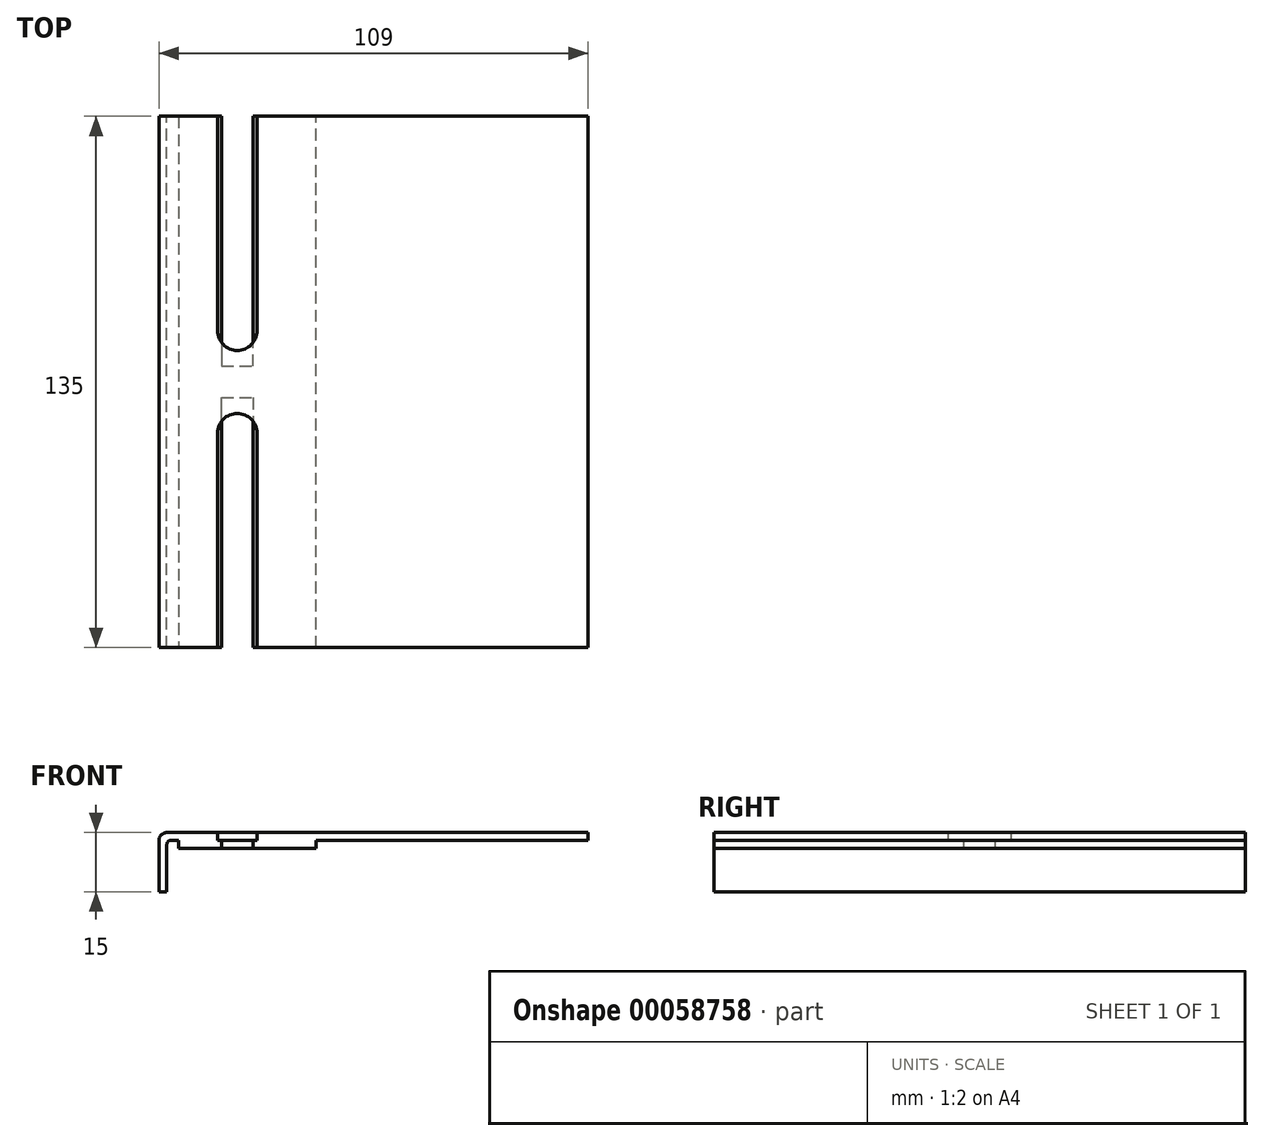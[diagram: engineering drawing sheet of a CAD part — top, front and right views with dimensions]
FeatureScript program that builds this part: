
annotation { "Feature Type Name" : "Feature", "Feature Type Description" : "" }
export const myFeature = defineFeature(function(context is Context, id is Id, definition is map)
    precondition{}
    {
        {
            var Q0;
            Q0=qCreatedBy(makeId("Front.planeOp"),FACE);
            var sketch = newSketch(context, id + "F0", { "sketchPlane" : qUnion([Q0])});
            skLineSegment(sketch, "E0.rect.bottom", {"start": v(54.5, -1) * mm, "end": v(-51.5, -1) * mm});
            skLineSegment(sketch, "E0.rect.top", {"start": v(54.5, 1) * mm, "end": v(-52.5, 1) * mm});
            skLineSegment(sketch, "E0.rect.left", {"start": v(54.5, -1) * mm, "end": v(54.5, 1) * mm});
            skPoint(sketch, "E0.rect.middle", {"position": v(0, 0) * mm});
            skLineSegment(sketch, "E1.top", {"start": v(-54.5, -14) * mm, "end": v(-52.5, -14) * mm});
            skLineSegment(sketch, "E1.right", {"start": v(-52.5, -2) * mm, "end": v(-52.5, -14) * mm});
            skLineSegment(sketch, "E2", {"start": v(-54.5, -1) * mm, "end": v(-54.5, -14) * mm});
            skPoint(sketch, "E3.visualSharp", {"position": v(-54.5, 1) * mm});
            skArc(sketch, "E3.filletArc", {"start": v(-52.5, 1) * mm, "mid": v(-53.91, 0.41) * mm, "end": v(-54.5, -1) * mm});
            skArc(sketch, "E4.filletArc", {"start": v(-51.5, -1) * mm, "mid": v(-52.2, -1.3) * mm, "end": v(-52.5, -2) * mm});
            skSolve(sketch);
        }
        {
            var Q0;
            Q0=makeQuery(id+"F0.imprint","IMPRINT",FACE,{"disambiguationData":[TD([[makeQuery(id+"F0.imprint","IMPRINT",EDGE,{"derivedFrom":sQuery(id+"F0.wireOp",EDGE,"E0.rect.bottom")}),-1.0]])]});
            extrude(context, id + "F1", {"entities" : qUnion([Q0]), "depth" : 67.5 * mm, "hasSecondDirection" : true, "secondDirectionOppositeDirection" : true, "secondDirectionDepth" : 67.5 * mm});
        }
        {
            var Q0;
            Q0=makeQuery(id+"F1.opExtrude","SWEPT_FACE",FACE,{"disambiguationData":[OSD([sQuery(id+"F0.wireOp",EDGE,"E0.rect.top")])]});
            var sketch = newSketch(context, id + "F2", { "sketchPlane" : qUnion([Q0])});
            skLineSegment(sketch, "E5.bottom", {"start": v(-34.6, 8) * mm, "end": v(-34.6, 8) * mm});
            skLineSegment(sketch, "E5.top", {"start": v(-39.6, 67.5) * mm, "end": v(-29.6, 67.5) * mm});
            skLineSegment(sketch, "E5.left", {"start": v(-39.6, 13) * mm, "end": v(-39.6, 67.5) * mm});
            skLineSegment(sketch, "E5.right", {"start": v(-29.6, 13) * mm, "end": v(-29.6, 67.5) * mm});
            skLineSegment(sketch, "E6.bottom", {"start": v(-34.6, -8) * mm, "end": v(-34.6, -8) * mm});
            skLineSegment(sketch, "E6.top", {"start": v(-39.6, -67.5) * mm, "end": v(-29.6, -67.5) * mm});
            skLineSegment(sketch, "E6.left", {"start": v(-39.6, -13) * mm, "end": v(-39.6, -67.5) * mm});
            skLineSegment(sketch, "E6.right", {"start": v(-29.6, -13) * mm, "end": v(-29.6, -67.5) * mm});
            skPoint(sketch, "E7.visualSharp", {"position": v(-39.6, 8) * mm});
            skArc(sketch, "E7.filletArc", {"start": v(-39.6, 13) * mm, "mid": v(-38.14, 9.46) * mm, "end": v(-34.6, 8) * mm});
            skPoint(sketch, "E8.visualSharp", {"position": v(-29.6, 8) * mm});
            skArc(sketch, "E8.filletArc", {"start": v(-34.6, 8) * mm, "mid": v(-31.06, 9.46) * mm, "end": v(-29.6, 13) * mm});
            skPoint(sketch, "E9.visualSharp", {"position": v(-39.6, -8) * mm});
            skArc(sketch, "E9.filletArc", {"start": v(-34.6, -8) * mm, "mid": v(-38.14, -9.46) * mm, "end": v(-39.6, -13) * mm});
            skPoint(sketch, "E10.visualSharp", {"position": v(-29.6, -8) * mm});
            skArc(sketch, "E10.filletArc", {"start": v(-29.6, -13) * mm, "mid": v(-31.06, -9.46) * mm, "end": v(-34.6, -8) * mm});
            skSolve(sketch);
        }
        {
            var Q0;
            Q0=makeQuery(id+"F2.imprint","IMPRINT",FACE,{"disambiguationData":[TD([[makeQuery(id+"F2.imprint","IMPRINT",EDGE,{"derivedFrom":sQuery(id+"F2.wireOp",EDGE,"E6.top")}),-1.0]])]});
            var Q1;
            Q1=makeQuery(id+"F2.imprint","IMPRINT",FACE,{"disambiguationData":[TD([[makeQuery(id+"F2.imprint","IMPRINT",EDGE,{"derivedFrom":sQuery(id+"F2.wireOp",EDGE,"E5.top")}),1.0]])]});
            extrude(context, id + "F3", {"entities" : qUnion([Q0, Q1]), "operationType" : NewBodyOperationType.REMOVE, "endBound" : BoundingType.THROUGH_ALL, "oppositeDirection" : true, "depth" : 25 * mm});
        }
        {
            var Q0;
            Q0=makeQuery(id+"F1.opExtrude","SWEPT_FACE",FACE,{"disambiguationData":[OSD([sQuery(id+"F0.wireOp",EDGE,"E0.rect.bottom")])]});
            var sketch = newSketch(context, id + "F4", { "sketchPlane" : qUnion([Q0])});
            skLineSegment(sketch, "E11", {"start": v(-49.5, 67.5) * mm, "end": v(-38.6, 67.5) * mm});
            skLineSegment(sketch, "E12", {"start": v(-38.6, 67.5) * mm, "end": v(-38.6, 4) * mm});
            skLineSegment(sketch, "E13", {"start": v(-38.6, 4) * mm, "end": v(-30.6, 4) * mm});
            skLineSegment(sketch, "E14", {"start": v(-30.6, 4) * mm, "end": v(-30.6, 67.5) * mm});
            skLineSegment(sketch, "E15", {"start": v(-30.6, 67.5) * mm, "end": v(-14.6, 67.5) * mm});
            skLineSegment(sketch, "E16", {"start": v(-14.6, 67.5) * mm, "end": v(-14.6, 0) * mm});
            skLineSegment(sketch, "E17", {"start": v(-14.6, 0) * mm, "end": v(-49.5, 0) * mm});
            skLineSegment(sketch, "E18", {"start": v(-49.5, 0) * mm, "end": v(-49.5, 67.5) * mm});
            skSolve(sketch);
        }
        {
            var Q0;
            {var subQ16=sQuery(id+"F4.wireOp",EDGE,"E13");Q0=makeQuery(id+"F4.imprint","IMPRINT",FACE,{"disambiguationData":[TD([[makeQuery(id+"F4.imprint","IMPRINT",EDGE,{"derivedFrom":subQ16}),-1.0]])]});}
            var Q1;
            {var subQ1=makeQuery(id+"F1.opExtrude","SWEPT_FACE",FACE,{"disambiguationData":[OSD([sQuery(id+"F0.wireOp",EDGE,"E0.rect.bottom")])]});var subQ2=makeQuery(id+"F3.boolean.opBoolean","INTERSECT",EDGE,{"derivedFrom":[subQ1,makeQuery(id+"F3.opExtrude","SWEPT_FACE",FACE,{"disambiguationData":[OSD([sQuery(id+"F2.wireOp",EDGE,"E6.left")])]})]});Q1=makeQuery(id+"F4.imprint","IMPRINT",FACE,{"disambiguationData":[TD([[makeQuery(id+"F4.imprint","IMPRINT",EDGE,{"derivedFrom":subQ2}),1.0]])]});}
            var Q2;
            {var subQ3=makeQuery(id+"F1.opExtrude","SWEPT_FACE",FACE,{"disambiguationData":[OSD([sQuery(id+"F0.wireOp",EDGE,"E0.rect.bottom")])]});var subQ6=makeQuery(id+"F3.boolean.opBoolean","INTERSECT",EDGE,{"derivedFrom":[subQ3,makeQuery(id+"F3.opExtrude","SWEPT_FACE",FACE,{"disambiguationData":[OSD([sQuery(id+"F2.wireOp",EDGE,"E6.right")])]})]});Q2=makeQuery(id+"F4.imprint","IMPRINT",FACE,{"disambiguationData":[TD([[makeQuery(id+"F4.imprint","IMPRINT",EDGE,{"derivedFrom":subQ6}),-1.0]])]});}
            extrude(context, id + "F5", {"entities" : qUnion([Q0, Q1, Q2]), "depth" : 2 * mm});
        }
        {
            var Q0;
            Q0=makeQuery(id+"F5.opExtrude","SWEPT_BODY",BODY,{"disambiguationData":[OSD([sQuery(id+"F4.wireOp",EDGE,"E11"),sQuery(id+"F4.wireOp",EDGE,"E12"),sQuery(id+"F4.wireOp",EDGE,"E13"),sQuery(id+"F4.wireOp",EDGE,"E14"),sQuery(id+"F4.wireOp",EDGE,"E15"),sQuery(id+"F4.wireOp",EDGE,"E16"),sQuery(id+"F4.wireOp",EDGE,"E17"),sQuery(id+"F4.wireOp",EDGE,"E18")])]});
            var Q1;
            Q1=qCreatedBy(makeId("Front.planeOp"),FACE);
            mirror(context, id + "F6", {"operationType" : NewBodyOperationType.ADD, "entities" : qUnion([Q0]), "mirrorPlane" : qUnion([Q1])});
        }
    });
